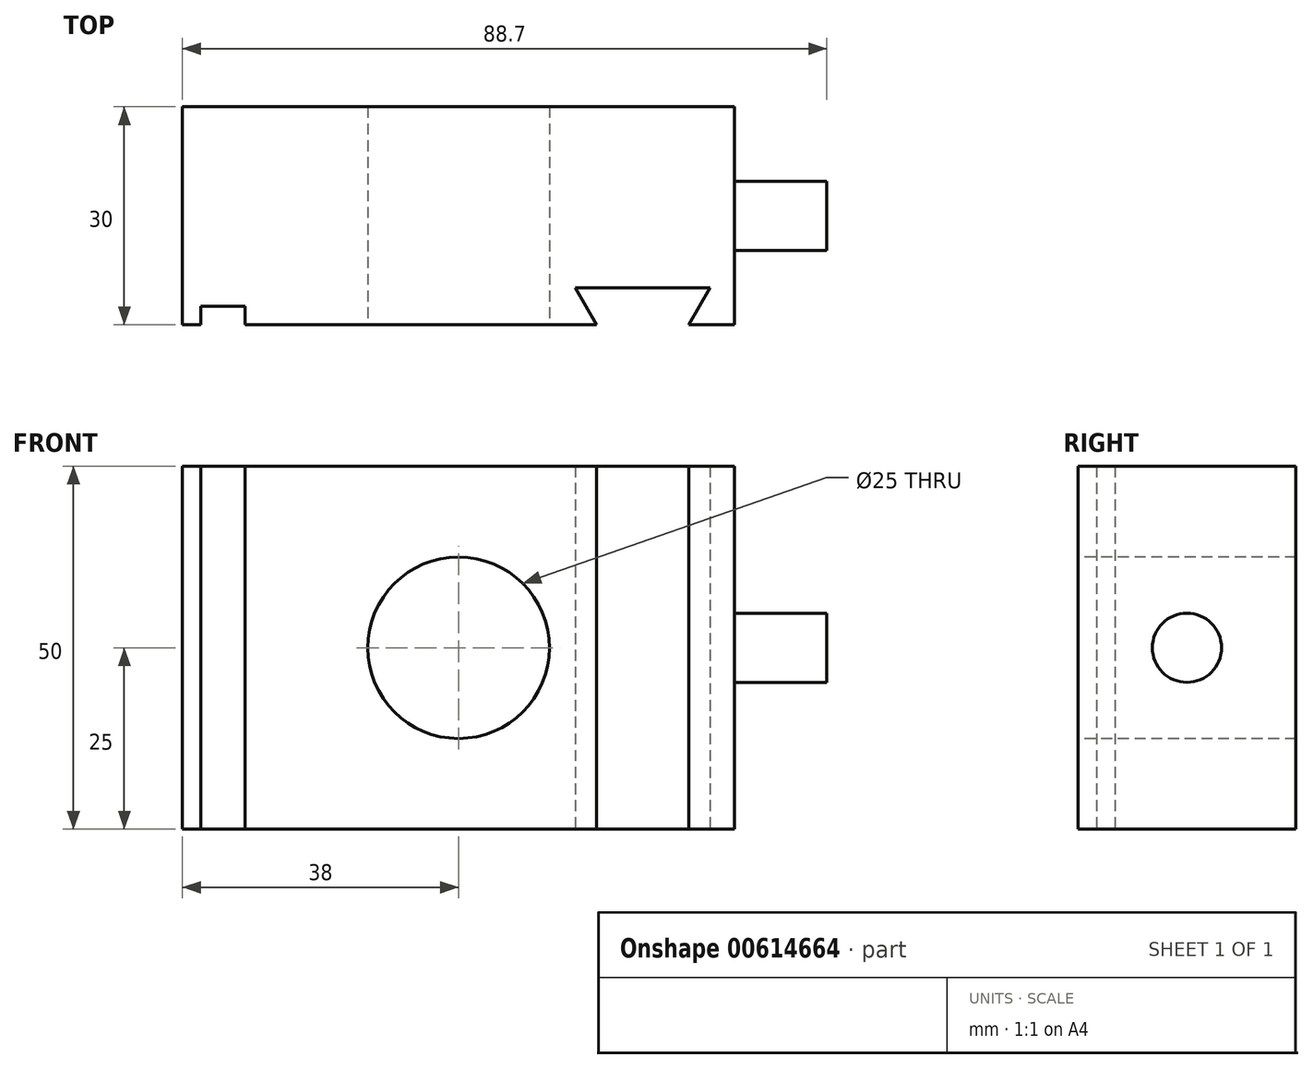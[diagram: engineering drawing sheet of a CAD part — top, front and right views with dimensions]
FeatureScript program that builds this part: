
annotation { "Feature Type Name" : "Feature", "Feature Type Description" : "" }
export const myFeature = defineFeature(function(context is Context, id is Id, definition is map)
    precondition{}
    {
        {
            var Q0;
            Q0=qCreatedBy(makeId("Front.planeOp"),FACE);
            var sketch = newSketch(context, id + "F0", { "sketchPlane" : qUnion([Q0])});
            skLineSegment(sketch, "E0.bottom", {"start": v(38, 25) * mm, "end": v(-38, 25) * mm});
            skLineSegment(sketch, "E0.top", {"start": v(38, -25) * mm, "end": v(-38, -25) * mm});
            skLineSegment(sketch, "E0.left", {"start": v(38, 25) * mm, "end": v(38, -25) * mm});
            skLineSegment(sketch, "E0.right", {"start": v(-38, 25) * mm, "end": v(-38, -25) * mm});
            skPoint(sketch, "E0.middle", {"position": v(0, 0) * mm});
            skSolve(sketch);
        }
        {
            var Q0;
            Q0=makeQuery(id+"F0.imprint","IMPRINT",FACE,{"disambiguationData":[TD([[makeQuery(id+"F0.imprint","IMPRINT",EDGE,{"derivedFrom":sQuery(id+"F0.wireOp",EDGE,"E0.bottom")}),1.0]])]});
            extrude(context, id + "F1", {"entities" : qUnion([Q0]), "depth" : 30 * mm, "offsetDistance" : 25 * mm});
        }
        {
            var Q0;
            Q0=makeQuery(id+"F1.opExtrude","CAP_FACE",FACE,{"disambiguationData":[OSD([sQuery(id+"F0.wireOp",EDGE,"E0.bottom"),sQuery(id+"F0.wireOp",EDGE,"E0.top"),sQuery(id+"F0.wireOp",EDGE,"E0.left"),sQuery(id+"F0.wireOp",EDGE,"E0.right")])],"isStart":false});
            var sketch = newSketch(context, id + "F2", { "sketchPlane" : qUnion([Q0])});
            skCircle(sketch, "E1", {"center": v(0, 0) * mm, "radius": 12.5 * mm});
            skSolve(sketch);
        }
        {
            var Q0;
            Q0=makeQuery(id+"F2.imprint","IMPRINT",FACE,{"disambiguationData":[TD([[makeQuery(id+"F2.imprint","IMPRINT",EDGE,{"derivedFrom":sQuery(id+"F2.wireOp",EDGE,"E1")}),1.0]])]});
            var sketch = newSketch(context, id + "F3", { "sketchPlane" : qUnion([Q0])});
            skSolve(sketch);
        }
        {
            var Q0;
            Q0=makeQuery(id+"F3.imprint","IMPRINT",FACE,{"disambiguationData":[TD([[makeQuery(id+"F3.imprint","IMPRINT",EDGE,{"derivedFrom":makeQuery(id+"F2.imprint","IMPRINT",EDGE,{"derivedFrom":sQuery(id+"F2.wireOp",EDGE,"E1")})}),1.0]])]});
            var Q1;
            Q1=sQuery(id+"F2.wireOp",EDGE,"E1");
            extrude(context, id + "F4", {"entities" : qUnion([Q0]), "operationType" : NewBodyOperationType.REMOVE, "surfaceEntities" : qUnion([Q1]), "endBound" : BoundingType.THROUGH_ALL, "oppositeDirection" : true, "depth" : 40 * mm, "offsetDistance" : 25 * mm});
        }
        {
            var Q0;
            Q0=makeQuery(id+"F1.opExtrude","CAP_FACE",FACE,{"disambiguationData":[OSD([sQuery(id+"F0.wireOp",EDGE,"E0.bottom"),sQuery(id+"F0.wireOp",EDGE,"E0.top"),sQuery(id+"F0.wireOp",EDGE,"E0.left"),sQuery(id+"F0.wireOp",EDGE,"E0.right")])],"isStart":false});
            var sketch = newSketch(context, id + "F5", { "sketchPlane" : qUnion([Q0])});
            skLineSegment(sketch, "E2.bottom", {"start": v(-35.46, 25) * mm, "end": v(-29.36, 25) * mm});
            skLineSegment(sketch, "E2.top", {"start": v(-35.46, -25) * mm, "end": v(-29.36, -25) * mm});
            skLineSegment(sketch, "E2.left", {"start": v(-35.46, 25) * mm, "end": v(-35.46, -25) * mm});
            skLineSegment(sketch, "E2.right", {"start": v(-29.36, 25) * mm, "end": v(-29.36, -25) * mm});
            skSolve(sketch);
        }
        {
            var Q0;
            {var subQ2=sQuery(id+"F5.wireOp",EDGE,"E2.right");Q0=makeQuery(id+"F5.imprint","IMPRINT",FACE,{"disambiguationData":[TD([[makeQuery(id+"F5.imprint","IMPRINT",EDGE,{"derivedFrom":subQ2}),1.0]])]});}
            var sketch = newSketch(context, id + "F6", { "sketchPlane" : qUnion([Q0])});
            skLineSegment(sketch, "E3", {"start": v(-5.11, 27.75) * mm, "end": v(-5.11, -28.05) * mm});
            skLineSegment(sketch, "E4", {"start": v(-5.11, -28.05) * mm, "end": v(5.05, -28.05) * mm});
            skLineSegment(sketch, "E5", {"start": v(5.05, -28.05) * mm, "end": v(5.05, 27.75) * mm});
            skLineSegment(sketch, "E6", {"start": v(5.05, 27.75) * mm, "end": v(-5.11, 27.75) * mm});
            skLineSegment(sketch, "E7", {"start": v(-0.03, 27.75) * mm, "end": v(-0.03, -28.05) * mm, "construction": true});
            skSolve(sketch);
        }
        {
            var Q0;
            Q0=makeQuery(id+"F5.imprint","IMPRINT",FACE,{"disambiguationData":[TD([[makeQuery(id+"F5.imprint","IMPRINT",EDGE,{"derivedFrom":sQuery(id+"F5.wireOp",EDGE,"E2.bottom")}),1.0]])]});
            var Q1;
            {var subQ0=sQuery(id+"F6.wireOp",EDGE,"E3");var subQ4=makeQuery(id+"F5.imprint","IMPRINT",EDGE,{"derivedFrom":makeQuery(id+"F4.boolean.opBoolean","COPY",EDGE,{"derivedFrom":makeQuery(id+"F4.opExtrude","CAP_EDGE",EDGE,{"disambiguationData":[OSD([sQuery(id+"F2.wireOp",EDGE,"E1")])],"isStart":true})})});var subQ5=makeQuery(id+"F6.imprint","INTERSECT",VERTEX,{"disambiguationData":[OD(1.0)],"derivedFrom":[subQ4,subQ0]});Q1=makeQuery(id+"F6.imprint","IMPRINT",FACE,{"disambiguationData":[TD([[makeQuery(id+"F6.imprint","IMPRINT",EDGE,{"disambiguationData":[TD([[subQ5,-1.0]])],"derivedFrom":subQ4}),-1.0]])]});}
            var Q2;
            {var subQ0=sQuery(id+"F6.wireOp",EDGE,"E3");var subQ4=makeQuery(id+"F5.imprint","IMPRINT",EDGE,{"derivedFrom":makeQuery(id+"F4.boolean.opBoolean","COPY",EDGE,{"derivedFrom":makeQuery(id+"F4.opExtrude","CAP_EDGE",EDGE,{"disambiguationData":[OSD([sQuery(id+"F2.wireOp",EDGE,"E1")])],"isStart":true})})});var subQ5=makeQuery(id+"F6.imprint","INTERSECT",VERTEX,{"disambiguationData":[OD(0.0)],"derivedFrom":[subQ4,subQ0]});Q2=makeQuery(id+"F6.imprint","IMPRINT",FACE,{"disambiguationData":[TD([[makeQuery(id+"F6.imprint","IMPRINT",EDGE,{"disambiguationData":[TD([[subQ5,1.0]])],"derivedFrom":subQ4}),-1.0]])]});}
            extrude(context, id + "F7", {"entities" : qUnion([Q0, Q1, Q2]), "operationType" : NewBodyOperationType.REMOVE, "oppositeDirection" : true, "depth" : 2.54 * mm, "offsetDistance" : 25.4 * mm});
        }
        {
            var Q0;
            Q0=makeQuery(id+"F1.opExtrude","SWEPT_FACE",FACE,{"disambiguationData":[OSD([sQuery(id+"F0.wireOp",EDGE,"E0.top")])]});
            var sketch = newSketch(context, id + "F8", { "sketchPlane" : qUnion([Q0])});
            skLineSegment(sketch, "E8", {"start": v(19.02, 30) * mm, "end": v(16.08, 24.92) * mm});
            skLineSegment(sketch, "E9", {"start": v(16.08, 24.92) * mm, "end": v(34.65, 24.92) * mm});
            skLineSegment(sketch, "E10", {"start": v(34.65, 24.92) * mm, "end": v(31.72, 30) * mm});
            skLineSegment(sketch, "E11", {"start": v(31.72, 30) * mm, "end": v(19.02, 30) * mm});
            skLineSegment(sketch, "E12", {"start": v(25.37, 24.92) * mm, "end": v(25.37, 30) * mm, "construction": true});
            skSolve(sketch);
        }
        {
            var Q0;
            Q0=makeQuery(id+"F8.imprint","IMPRINT",FACE,{"disambiguationData":[TD([[makeQuery(id+"F8.imprint","IMPRINT",EDGE,{"derivedFrom":sQuery(id+"F8.wireOp",EDGE,"E8")}),1.0]])]});
            extrude(context, id + "F9", {"entities" : qUnion([Q0]), "operationType" : NewBodyOperationType.REMOVE, "endBound" : BoundingType.THROUGH_ALL, "oppositeDirection" : true, "depth" : 25.4 * mm, "offsetDistance" : 25.4 * mm});
        }
        {
            var Q0;
            Q0=makeQuery(id+"F1.opExtrude","SWEPT_FACE",FACE,{"disambiguationData":[OSD([sQuery(id+"F0.wireOp",EDGE,"E0.left")])]});
            var sketch = newSketch(context, id + "F10", { "sketchPlane" : qUnion([Q0])});
            skPoint(sketch, "E13", {"position": v(-30, 0) * mm});
            skPoint(sketch, "E14", {"position": v(-15, -25) * mm});
            skPoint(sketch, "E15", {"position": v(-15, 0) * mm});
            skCircle(sketch, "E16", {"center": v(-15, 0) * mm, "radius": 4.76 * mm});
            skSolve(sketch);
        }
        {
            var Q0;
            Q0=makeQuery(id+"F10.imprint","IMPRINT",FACE,{"disambiguationData":[TD([[makeQuery(id+"F10.imprint","IMPRINT",EDGE,{"derivedFrom":sQuery(id+"F10.wireOp",EDGE,"E16")}),1.0]])]});
            extrude(context, id + "F11", {"entities" : qUnion([Q0]), "operationType" : NewBodyOperationType.ADD, "depth" : 12.7 * mm, "offsetDistance" : 25.4 * mm});
        }
    });
